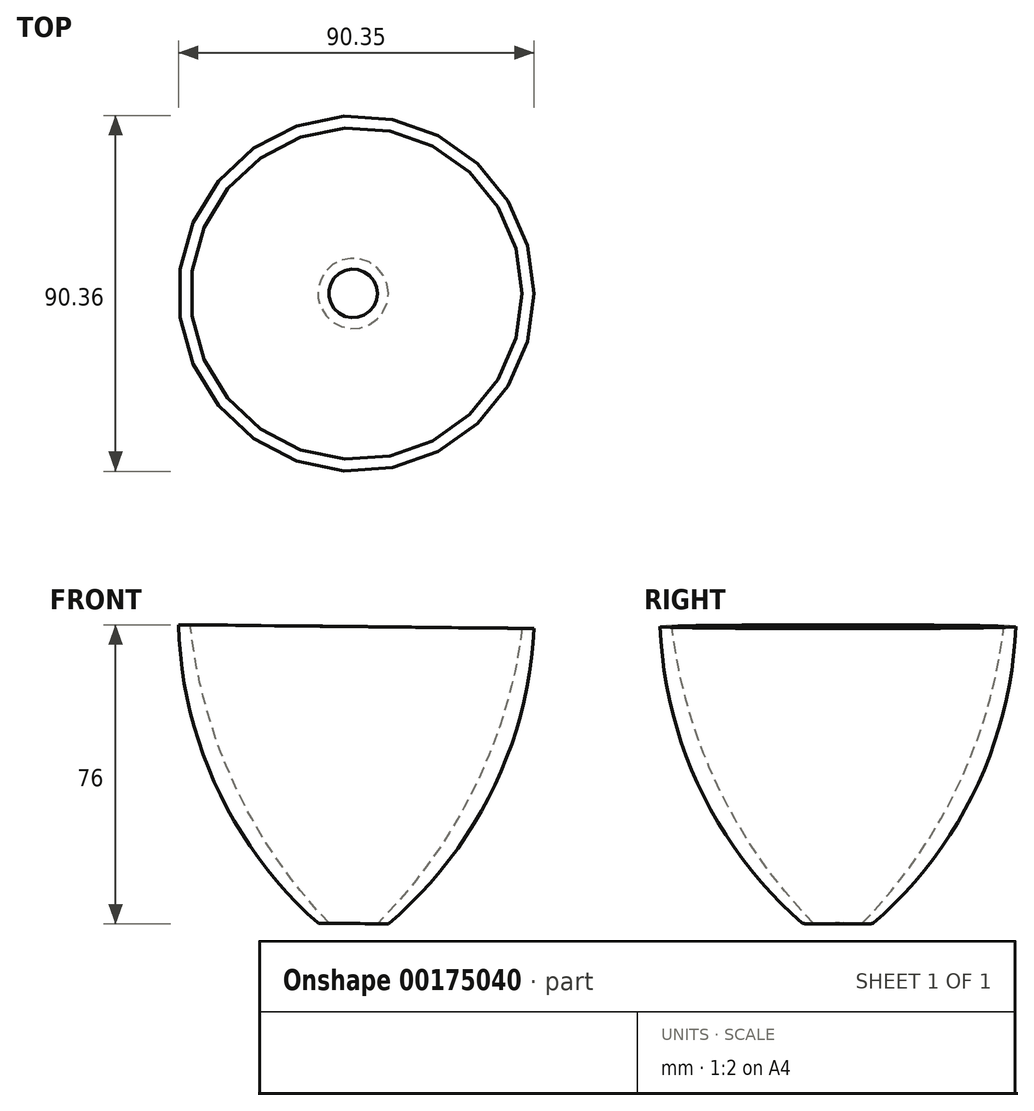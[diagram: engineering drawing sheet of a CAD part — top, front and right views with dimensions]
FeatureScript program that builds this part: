
annotation { "Feature Type Name" : "Feature", "Feature Type Description" : "" }
export const myFeature = defineFeature(function(context is Context, id is Id, definition is map)
    precondition{}
    {
        {
            var Q0;
            Q0=qCreatedBy(makeId("Front.planeOp"),FACE);
            var sketch = newSketch(context, id + "F0", { "sketchPlane" : qUnion([Q0])});
            skLineSegment(sketch, "E0", {"start": v(0, 30.99) * mm, "end": v(-1.2, -80.4) * mm});
            skArc(sketch, "E1", {"start": v(-45.55, -3.67) * mm, "mid": v(-35.7, -45.25) * mm, "end": v(-10.12, -79.47) * mm});
            skArc(sketch, "E2", {"start": v(-42.54, -3.67) * mm, "mid": v(-31.22, -44.49) * mm, "end": v(-7.35, -79.47) * mm});
            skLineSegment(sketch, "E3", {"start": v(-45.55, -3.67) * mm, "end": v(-42.54, -3.67) * mm});
            skLineSegment(sketch, "E4", {"start": v(-10.12, -79.47) * mm, "end": v(-7.35, -79.47) * mm});
            skSolve(sketch);
        }
        {
            var Q0;
            Q0 = qSketchRegion(id + "F0", true);
            var Q1;
            Q1=sQuery(id+"F0.wireOp",EDGE,"E0");
            revolve(context, id + "F1", {"entities" : qUnion([Q0]), "axis" : qUnion([Q1]), "revolveType" : RevolveType.FULL});
        }
    });
